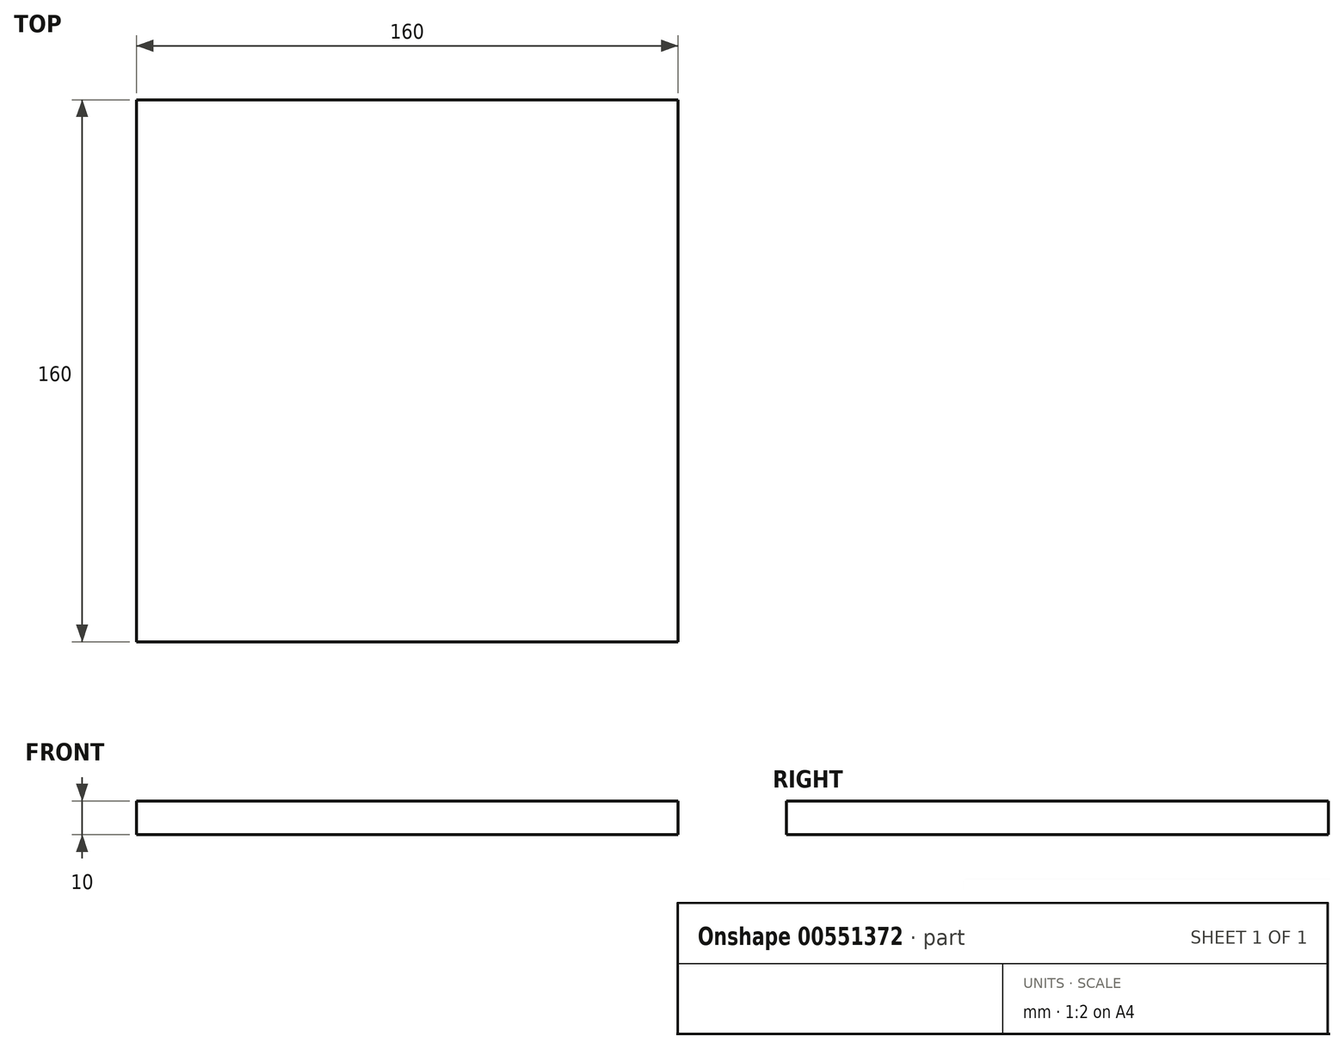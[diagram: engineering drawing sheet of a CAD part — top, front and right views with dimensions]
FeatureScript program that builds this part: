
annotation { "Feature Type Name" : "Feature", "Feature Type Description" : "" }
export const myFeature = defineFeature(function(context is Context, id is Id, definition is map)
    precondition{}
    {
        {
            var Q0;
            Q0=qCreatedBy(makeId("Top.planeOp"),FACE);
            var sketch = newSketch(context, id + "F0", { "sketchPlane" : qUnion([Q0])});
            skLineSegment(sketch, "E0.bottom", {"start": v(-80, 80) * mm, "end": v(80, 80) * mm});
            skLineSegment(sketch, "E0.top", {"start": v(-80, -80) * mm, "end": v(80, -80) * mm});
            skLineSegment(sketch, "E0.left", {"start": v(-80, 80) * mm, "end": v(-80, -80) * mm});
            skLineSegment(sketch, "E0.right", {"start": v(80, 80) * mm, "end": v(80, -80) * mm});
            skPoint(sketch, "E0.middle", {"position": v(0, 0) * mm});
            skSolve(sketch);
        }
        {
            var Q0;
            Q0 = qSketchRegion(id + "F0", true);
            extrude(context, id + "F1", {"entities" : qUnion([Q0]), "depth" : 10 * mm, "offsetDistance" : 25 * mm});
        }
    });
